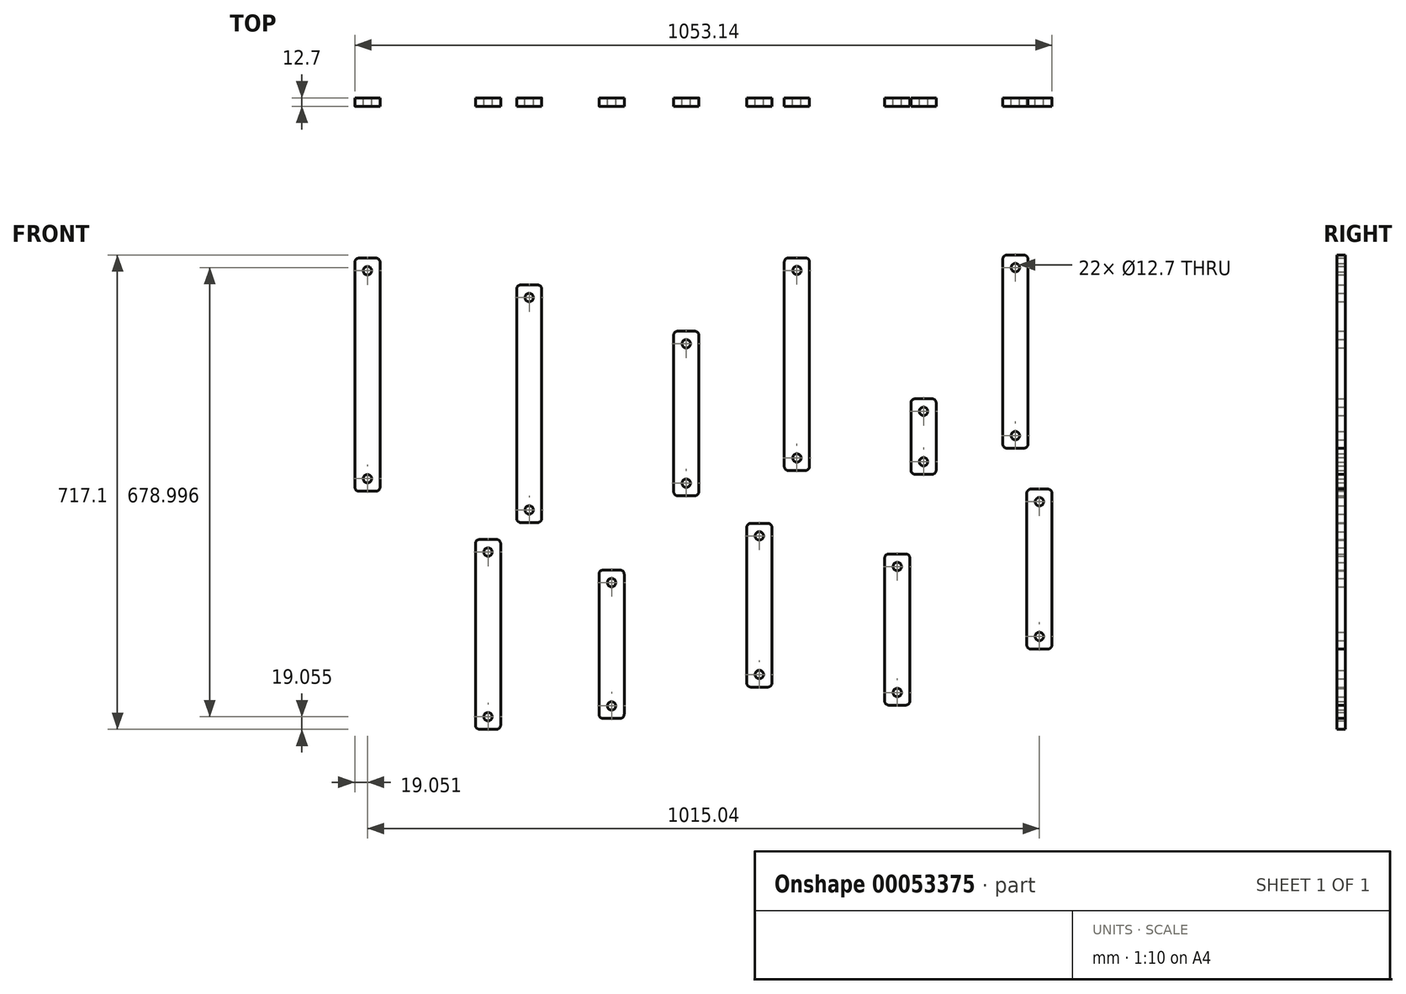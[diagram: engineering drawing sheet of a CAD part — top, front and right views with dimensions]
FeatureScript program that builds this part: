
annotation { "Feature Type Name" : "Feature", "Feature Type Description" : "" }
export const myFeature = defineFeature(function(context is Context, id is Id, definition is map)
    precondition{}
    {
        {
            var Q0;
            Q0=qCreatedBy(makeId("Front.planeOp"),FACE);
            var sketch = newSketch(context, id + "F0", { "sketchPlane" : qUnion([Q0])});
            skCircle(sketch, "E0", {"center": v(-240.16, 160.13) * mm, "radius": 6.35 * mm});
            skCircle(sketch, "E1", {"center": v(-240.16, -93.87) * mm, "radius": 6.35 * mm});
            skLineSegment(sketch, "E2.bottom", {"start": v(-252.86, 179.18) * mm, "end": v(-227.46, 179.18) * mm});
            skLineSegment(sketch, "E2.top", {"start": v(-252.86, -112.92) * mm, "end": v(-227.46, -112.92) * mm});
            skLineSegment(sketch, "E2.left", {"start": v(-259.2, 172.83) * mm, "end": v(-259.2, -106.57) * mm});
            skLineSegment(sketch, "E2.right", {"start": v(-221.1, 172.83) * mm, "end": v(-221.1, -106.57) * mm});
            skPoint(sketch, "E3.visualSharp", {"position": v(-221.1, 179.18) * mm});
            skArc(sketch, "E3.filletArc", {"start": v(-221.1, 172.83) * mm, "mid": v(-222.97, 177.32) * mm, "end": v(-227.46, 179.18) * mm});
            skPoint(sketch, "E4.visualSharp", {"position": v(-259.2, 179.18) * mm});
            skArc(sketch, "E4.filletArc", {"start": v(-252.86, 179.18) * mm, "mid": v(-257.35, 177.32) * mm, "end": v(-259.2, 172.83) * mm});
            skPoint(sketch, "E5.visualSharp", {"position": v(-221.1, -112.92) * mm});
            skArc(sketch, "E5.filletArc", {"start": v(-227.46, -112.92) * mm, "mid": v(-222.97, -111.06) * mm, "end": v(-221.1, -106.57) * mm});
            skPoint(sketch, "E6.visualSharp", {"position": v(-259.2, -112.92) * mm});
            skArc(sketch, "E6.filletArc", {"start": v(-259.2, -106.57) * mm, "mid": v(-257.35, -111.06) * mm, "end": v(-252.86, -112.92) * mm});
            skLineSegment(sketch, "E7.right", {"start": v(-359.88, -44.47) * mm, "end": v(-359.88, -146.07) * mm});
            skLineSegment(sketch, "E7.left", {"start": v(-397.98, -44.47) * mm, "end": v(-397.98, -146.07) * mm});
            skPoint(sketch, "E8.visualSharp", {"position": v(-359.88, -38.12) * mm});
            skLineSegment(sketch, "E7.top", {"start": v(-391.63, -152.42) * mm, "end": v(-366.23, -152.42) * mm});
            skLineSegment(sketch, "E7.bottom", {"start": v(-391.63, -38.12) * mm, "end": v(-366.23, -38.12) * mm});
            skPoint(sketch, "E9.visualSharp", {"position": v(-397.98, -38.12) * mm});
            skCircle(sketch, "E10", {"center": v(-378.93, -133.37) * mm, "radius": 6.35 * mm});
            skCircle(sketch, "E11", {"center": v(-378.93, -57.17) * mm, "radius": 6.35 * mm});
            skPoint(sketch, "E12.visualSharp", {"position": v(-359.88, -152.42) * mm});
            skPoint(sketch, "E13.visualSharp", {"position": v(-397.98, -152.42) * mm});
            skArc(sketch, "E12.filletArc", {"start": v(-366.23, -152.42) * mm, "mid": v(-361.74, -150.56) * mm, "end": v(-359.88, -146.07) * mm});
            skArc(sketch, "E9.filletArc", {"start": v(-391.63, -38.12) * mm, "mid": v(-396.12, -39.98) * mm, "end": v(-397.98, -44.47) * mm});
            skArc(sketch, "E8.filletArc", {"start": v(-359.88, -44.47) * mm, "mid": v(-361.74, -39.98) * mm, "end": v(-366.23, -38.12) * mm});
            skArc(sketch, "E13.filletArc", {"start": v(-397.98, -146.07) * mm, "mid": v(-396.12, -150.56) * mm, "end": v(-391.63, -152.42) * mm});
            skPoint(sketch, "E14.visualSharp", {"position": v(-589.26, -146.73) * mm});
            skPoint(sketch, "E15.visualSharp", {"position": v(-551.16, -146.73) * mm});
            skPoint(sketch, "E16.visualSharp", {"position": v(-589.26, 174.84) * mm});
            skLineSegment(sketch, "E17.left", {"start": v(-589.26, 168.49) * mm, "end": v(-589.26, -140.38) * mm});
            skLineSegment(sketch, "E17.right", {"start": v(-551.16, 168.49) * mm, "end": v(-551.16, -140.38) * mm});
            skPoint(sketch, "E18.visualSharp", {"position": v(-551.16, 174.84) * mm});
            skCircle(sketch, "E19", {"center": v(-570.2, 155.79) * mm, "radius": 6.35 * mm});
            skLineSegment(sketch, "E17.top", {"start": v(-582.9, -146.73) * mm, "end": v(-557.5, -146.73) * mm});
            skCircle(sketch, "E20", {"center": v(-570.2, -127.68) * mm, "radius": 6.35 * mm});
            skLineSegment(sketch, "E17.bottom", {"start": v(-582.9, 174.84) * mm, "end": v(-557.5, 174.84) * mm});
            skArc(sketch, "E16.filletArc", {"start": v(-582.9, 174.84) * mm, "mid": v(-587.4, 172.98) * mm, "end": v(-589.26, 168.49) * mm});
            skArc(sketch, "E18.filletArc", {"start": v(-551.16, 168.49) * mm, "mid": v(-553.02, 172.98) * mm, "end": v(-557.5, 174.84) * mm});
            skArc(sketch, "E15.filletArc", {"start": v(-557.5, -146.73) * mm, "mid": v(-553.02, -144.87) * mm, "end": v(-551.16, -140.38) * mm});
            skArc(sketch, "E14.filletArc", {"start": v(-589.26, -140.38) * mm, "mid": v(-587.4, -144.87) * mm, "end": v(-582.9, -146.73) * mm});
            skPoint(sketch, "E21.visualSharp", {"position": v(-756.47, -184.84) * mm});
            skPoint(sketch, "E22.visualSharp", {"position": v(-718.37, -184.84) * mm});
            skPoint(sketch, "E23.visualSharp", {"position": v(-756.47, 64.08) * mm});
            skLineSegment(sketch, "E24.left", {"start": v(-756.47, 57.73) * mm, "end": v(-756.47, -178.49) * mm});
            skLineSegment(sketch, "E24.right", {"start": v(-718.37, 57.73) * mm, "end": v(-718.37, -178.49) * mm});
            skPoint(sketch, "E25.visualSharp", {"position": v(-718.37, 64.08) * mm});
            skCircle(sketch, "E26", {"center": v(-737.42, 45.03) * mm, "radius": 6.35 * mm});
            skLineSegment(sketch, "E24.top", {"start": v(-750.12, -184.84) * mm, "end": v(-724.72, -184.84) * mm});
            skCircle(sketch, "E27", {"center": v(-737.42, -165.79) * mm, "radius": 6.35 * mm});
            skLineSegment(sketch, "E24.bottom", {"start": v(-750.12, 64.08) * mm, "end": v(-724.72, 64.08) * mm});
            skArc(sketch, "E23.filletArc", {"start": v(-750.12, 64.08) * mm, "mid": v(-754.6, 62.22) * mm, "end": v(-756.47, 57.73) * mm});
            skArc(sketch, "E25.filletArc", {"start": v(-718.37, 57.73) * mm, "mid": v(-720.23, 62.22) * mm, "end": v(-724.72, 64.08) * mm});
            skArc(sketch, "E22.filletArc", {"start": v(-724.72, -184.84) * mm, "mid": v(-720.23, -182.98) * mm, "end": v(-718.37, -178.49) * mm});
            skArc(sketch, "E21.filletArc", {"start": v(-756.47, -178.49) * mm, "mid": v(-754.6, -182.98) * mm, "end": v(-750.12, -184.84) * mm});
            skPoint(sketch, "E28.visualSharp", {"position": v(-222.96, -416.6) * mm});
            skPoint(sketch, "E29.visualSharp", {"position": v(-184.86, -416.6) * mm});
            skPoint(sketch, "E30.visualSharp", {"position": v(-222.96, -174.78) * mm});
            skLineSegment(sketch, "E31.left", {"start": v(-222.96, -181.13) * mm, "end": v(-222.96, -410.24) * mm});
            skLineSegment(sketch, "E31.right", {"start": v(-184.86, -181.13) * mm, "end": v(-184.86, -410.24) * mm});
            skPoint(sketch, "E32.visualSharp", {"position": v(-184.86, -174.78) * mm});
            skCircle(sketch, "E33", {"center": v(-203.9, -193.83) * mm, "radius": 6.35 * mm});
            skLineSegment(sketch, "E31.top", {"start": v(-216.6, -416.6) * mm, "end": v(-191.2, -416.6) * mm});
            skCircle(sketch, "E34", {"center": v(-203.9, -397.54) * mm, "radius": 6.35 * mm});
            skLineSegment(sketch, "E31.bottom", {"start": v(-216.6, -174.78) * mm, "end": v(-191.2, -174.78) * mm});
            skArc(sketch, "E30.filletArc", {"start": v(-216.6, -174.78) * mm, "mid": v(-221.1, -176.64) * mm, "end": v(-222.96, -181.13) * mm});
            skArc(sketch, "E32.filletArc", {"start": v(-184.86, -181.13) * mm, "mid": v(-186.72, -176.64) * mm, "end": v(-191.2, -174.78) * mm});
            skArc(sketch, "E29.filletArc", {"start": v(-191.2, -416.6) * mm, "mid": v(-186.72, -414.73) * mm, "end": v(-184.86, -410.24) * mm});
            skArc(sketch, "E28.filletArc", {"start": v(-222.96, -410.24) * mm, "mid": v(-221.1, -414.73) * mm, "end": v(-216.6, -416.6) * mm});
            skPoint(sketch, "E35.visualSharp", {"position": v(-437.6, -501.36) * mm});
            skPoint(sketch, "E36.visualSharp", {"position": v(-399.5, -501.36) * mm});
            skPoint(sketch, "E37.visualSharp", {"position": v(-437.6, -272.76) * mm});
            skLineSegment(sketch, "E38.left", {"start": v(-437.6, -279.11) * mm, "end": v(-437.6, -495.01) * mm});
            skLineSegment(sketch, "E38.right", {"start": v(-399.5, -279.11) * mm, "end": v(-399.5, -495.01) * mm});
            skPoint(sketch, "E39.visualSharp", {"position": v(-399.5, -272.76) * mm});
            skCircle(sketch, "E40", {"center": v(-418.56, -291.81) * mm, "radius": 6.35 * mm});
            skLineSegment(sketch, "E38.top", {"start": v(-431.26, -501.36) * mm, "end": v(-405.86, -501.36) * mm});
            skCircle(sketch, "E41", {"center": v(-418.56, -482.31) * mm, "radius": 6.35 * mm});
            skLineSegment(sketch, "E38.bottom", {"start": v(-431.26, -272.76) * mm, "end": v(-405.86, -272.76) * mm});
            skArc(sketch, "E37.filletArc", {"start": v(-431.26, -272.76) * mm, "mid": v(-435.75, -274.62) * mm, "end": v(-437.6, -279.11) * mm});
            skArc(sketch, "E39.filletArc", {"start": v(-399.5, -279.11) * mm, "mid": v(-401.37, -274.62) * mm, "end": v(-405.86, -272.76) * mm});
            skArc(sketch, "E36.filletArc", {"start": v(-405.86, -501.36) * mm, "mid": v(-401.37, -499.5) * mm, "end": v(-399.5, -495.01) * mm});
            skArc(sketch, "E35.filletArc", {"start": v(-437.6, -495.01) * mm, "mid": v(-435.75, -499.5) * mm, "end": v(-431.26, -501.36) * mm});
            skPoint(sketch, "E42.visualSharp", {"position": v(-646.03, -474.14) * mm});
            skPoint(sketch, "E43.visualSharp", {"position": v(-607.93, -474.14) * mm});
            skPoint(sketch, "E44.visualSharp", {"position": v(-646.03, -226.5) * mm});
            skLineSegment(sketch, "E45.left", {"start": v(-646.03, -232.84) * mm, "end": v(-646.03, -467.8) * mm});
            skLineSegment(sketch, "E45.right", {"start": v(-607.93, -232.84) * mm, "end": v(-607.93, -467.8) * mm});
            skPoint(sketch, "E46.visualSharp", {"position": v(-607.93, -226.5) * mm});
            skCircle(sketch, "E47", {"center": v(-626.98, -245.54) * mm, "radius": 6.35 * mm});
            skLineSegment(sketch, "E45.top", {"start": v(-639.68, -474.14) * mm, "end": v(-614.28, -474.14) * mm});
            skCircle(sketch, "E48", {"center": v(-626.98, -455.1) * mm, "radius": 6.35 * mm});
            skLineSegment(sketch, "E45.bottom", {"start": v(-639.68, -226.5) * mm, "end": v(-614.28, -226.5) * mm});
            skArc(sketch, "E44.filletArc", {"start": v(-639.68, -226.5) * mm, "mid": v(-644.17, -228.35) * mm, "end": v(-646.03, -232.84) * mm});
            skArc(sketch, "E46.filletArc", {"start": v(-607.93, -232.84) * mm, "mid": v(-609.8, -228.35) * mm, "end": v(-614.28, -226.5) * mm});
            skArc(sketch, "E43.filletArc", {"start": v(-614.28, -474.14) * mm, "mid": v(-609.8, -472.28) * mm, "end": v(-607.93, -467.8) * mm});
            skArc(sketch, "E42.filletArc", {"start": v(-646.03, -467.8) * mm, "mid": v(-644.17, -472.28) * mm, "end": v(-639.68, -474.14) * mm});
            skPoint(sketch, "E49.visualSharp", {"position": v(-869.23, -521.58) * mm});
            skPoint(sketch, "E50.visualSharp", {"position": v(-831.13, -521.58) * mm});
            skPoint(sketch, "E51.visualSharp", {"position": v(-869.23, -297.05) * mm});
            skLineSegment(sketch, "E52.left", {"start": v(-869.23, -303.4) * mm, "end": v(-869.23, -515.23) * mm});
            skLineSegment(sketch, "E52.right", {"start": v(-831.13, -303.4) * mm, "end": v(-831.13, -515.23) * mm});
            skPoint(sketch, "E53.visualSharp", {"position": v(-831.13, -297.05) * mm});
            skCircle(sketch, "E54", {"center": v(-850.18, -316.1) * mm, "radius": 6.35 * mm});
            skLineSegment(sketch, "E52.top", {"start": v(-862.88, -521.58) * mm, "end": v(-837.48, -521.58) * mm});
            skCircle(sketch, "E55", {"center": v(-850.18, -502.53) * mm, "radius": 6.35 * mm});
            skLineSegment(sketch, "E52.bottom", {"start": v(-862.88, -297.05) * mm, "end": v(-837.48, -297.05) * mm});
            skArc(sketch, "E51.filletArc", {"start": v(-862.88, -297.05) * mm, "mid": v(-867.37, -298.9) * mm, "end": v(-869.23, -303.4) * mm});
            skArc(sketch, "E53.filletArc", {"start": v(-831.13, -303.4) * mm, "mid": v(-833, -298.9) * mm, "end": v(-837.48, -297.05) * mm});
            skArc(sketch, "E50.filletArc", {"start": v(-837.48, -521.58) * mm, "mid": v(-833, -519.72) * mm, "end": v(-831.13, -515.23) * mm});
            skArc(sketch, "E49.filletArc", {"start": v(-869.23, -515.23) * mm, "mid": v(-867.37, -519.72) * mm, "end": v(-862.88, -521.58) * mm});
            skPoint(sketch, "E56.visualSharp", {"position": v(-993.67, -225.28) * mm});
            skPoint(sketch, "E57.visualSharp", {"position": v(-955.57, -225.28) * mm});
            skPoint(sketch, "E58.visualSharp", {"position": v(-993.67, 133.88) * mm});
            skLineSegment(sketch, "E59.left", {"start": v(-993.67, 127.53) * mm, "end": v(-993.67, -218.93) * mm});
            skLineSegment(sketch, "E59.right", {"start": v(-955.57, 127.53) * mm, "end": v(-955.57, -218.93) * mm});
            skPoint(sketch, "E60.visualSharp", {"position": v(-955.57, 133.88) * mm});
            skCircle(sketch, "E61", {"center": v(-974.62, 114.83) * mm, "radius": 6.35 * mm});
            skLineSegment(sketch, "E59.top", {"start": v(-987.32, -225.28) * mm, "end": v(-961.92, -225.28) * mm});
            skCircle(sketch, "E62", {"center": v(-974.62, -206.23) * mm, "radius": 6.35 * mm});
            skLineSegment(sketch, "E59.bottom", {"start": v(-987.32, 133.88) * mm, "end": v(-961.92, 133.88) * mm});
            skArc(sketch, "E58.filletArc", {"start": v(-987.32, 133.88) * mm, "mid": v(-991.8, 132.02) * mm, "end": v(-993.67, 127.53) * mm});
            skArc(sketch, "E60.filletArc", {"start": v(-955.57, 127.53) * mm, "mid": v(-957.43, 132.02) * mm, "end": v(-961.92, 133.88) * mm});
            skArc(sketch, "E57.filletArc", {"start": v(-961.92, -225.28) * mm, "mid": v(-957.43, -223.42) * mm, "end": v(-955.57, -218.93) * mm});
            skArc(sketch, "E56.filletArc", {"start": v(-993.67, -218.93) * mm, "mid": v(-991.8, -223.42) * mm, "end": v(-987.32, -225.28) * mm});
            skPoint(sketch, "E63.visualSharp", {"position": v(-1055.88, -537.92) * mm});
            skPoint(sketch, "E64.visualSharp", {"position": v(-1017.78, -537.92) * mm});
            skPoint(sketch, "E65.visualSharp", {"position": v(-1055.88, -250.9) * mm});
            skLineSegment(sketch, "E66.left", {"start": v(-1055.88, -257.25) * mm, "end": v(-1055.88, -531.57) * mm});
            skLineSegment(sketch, "E66.right", {"start": v(-1017.78, -257.25) * mm, "end": v(-1017.78, -531.57) * mm});
            skPoint(sketch, "E67.visualSharp", {"position": v(-1017.78, -250.9) * mm});
            skCircle(sketch, "E68", {"center": v(-1036.83, -269.95) * mm, "radius": 6.35 * mm});
            skLineSegment(sketch, "E66.top", {"start": v(-1049.53, -537.92) * mm, "end": v(-1024.13, -537.92) * mm});
            skCircle(sketch, "E69", {"center": v(-1036.83, -518.87) * mm, "radius": 6.35 * mm});
            skLineSegment(sketch, "E66.bottom", {"start": v(-1049.53, -250.9) * mm, "end": v(-1024.13, -250.9) * mm});
            skArc(sketch, "E65.filletArc", {"start": v(-1049.53, -250.9) * mm, "mid": v(-1054.02, -252.76) * mm, "end": v(-1055.88, -257.25) * mm});
            skArc(sketch, "E67.filletArc", {"start": v(-1017.78, -257.25) * mm, "mid": v(-1019.64, -252.76) * mm, "end": v(-1024.13, -250.9) * mm});
            skArc(sketch, "E64.filletArc", {"start": v(-1024.13, -537.92) * mm, "mid": v(-1019.64, -536.06) * mm, "end": v(-1017.78, -531.57) * mm});
            skArc(sketch, "E63.filletArc", {"start": v(-1055.88, -531.57) * mm, "mid": v(-1054.02, -536.06) * mm, "end": v(-1049.53, -537.92) * mm});
            skPoint(sketch, "E70.visualSharp", {"position": v(-1238, -178.06) * mm});
            skPoint(sketch, "E71.visualSharp", {"position": v(-1199.9, -178.06) * mm});
            skPoint(sketch, "E72.visualSharp", {"position": v(-1238, 174.5) * mm});
            skLineSegment(sketch, "E73.left", {"start": v(-1238, 168.15) * mm, "end": v(-1238, -171.7) * mm});
            skLineSegment(sketch, "E73.right", {"start": v(-1199.9, 168.15) * mm, "end": v(-1199.9, -171.7) * mm});
            skPoint(sketch, "E74.visualSharp", {"position": v(-1199.9, 174.5) * mm});
            skCircle(sketch, "E75", {"center": v(-1218.95, 155.45) * mm, "radius": 6.35 * mm});
            skLineSegment(sketch, "E73.top", {"start": v(-1231.65, -178.06) * mm, "end": v(-1206.25, -178.06) * mm});
            skCircle(sketch, "E76", {"center": v(-1218.95, -159) * mm, "radius": 6.35 * mm});
            skLineSegment(sketch, "E73.bottom", {"start": v(-1231.65, 174.5) * mm, "end": v(-1206.25, 174.5) * mm});
            skArc(sketch, "E72.filletArc", {"start": v(-1231.65, 174.5) * mm, "mid": v(-1236.14, 172.64) * mm, "end": v(-1238, 168.15) * mm});
            skArc(sketch, "E74.filletArc", {"start": v(-1199.9, 168.15) * mm, "mid": v(-1201.76, 172.64) * mm, "end": v(-1206.25, 174.5) * mm});
            skArc(sketch, "E71.filletArc", {"start": v(-1206.25, -178.06) * mm, "mid": v(-1201.76, -176.2) * mm, "end": v(-1199.9, -171.7) * mm});
            skArc(sketch, "E70.filletArc", {"start": v(-1238, -171.7) * mm, "mid": v(-1236.14, -176.2) * mm, "end": v(-1231.65, -178.06) * mm});
            skSolve(sketch);
        }
        {
            var Q0;
            Q0=makeQuery(id+"F0.imprint","IMPRINT",FACE,{"disambiguationData":[TD([[makeQuery(id+"F0.imprint","IMPRINT",EDGE,{"derivedFrom":sQuery(id+"F0.wireOp",EDGE,"E73.left")}),1.0]])]});
            var Q1;
            Q1=makeQuery(id+"F0.imprint","IMPRINT",FACE,{"disambiguationData":[TD([[makeQuery(id+"F0.imprint","IMPRINT",EDGE,{"derivedFrom":sQuery(id+"F0.wireOp",EDGE,"E59.left")}),1.0]])]});
            var Q2;
            Q2=makeQuery(id+"F0.imprint","IMPRINT",FACE,{"disambiguationData":[TD([[makeQuery(id+"F0.imprint","IMPRINT",EDGE,{"derivedFrom":sQuery(id+"F0.wireOp",EDGE,"E24.left")}),1.0]])]});
            var Q3;
            Q3=makeQuery(id+"F0.imprint","IMPRINT",FACE,{"disambiguationData":[TD([[makeQuery(id+"F0.imprint","IMPRINT",EDGE,{"derivedFrom":sQuery(id+"F0.wireOp",EDGE,"E17.left")}),1.0]])]});
            var Q4;
            Q4=makeQuery(id+"F0.imprint","IMPRINT",FACE,{"disambiguationData":[TD([[makeQuery(id+"F0.imprint","IMPRINT",EDGE,{"derivedFrom":sQuery(id+"F0.wireOp",EDGE,"E7.right")}),-1.0]])]});
            var Q5;
            Q5=makeQuery(id+"F0.imprint","IMPRINT",FACE,{"disambiguationData":[TD([[makeQuery(id+"F0.imprint","IMPRINT",EDGE,{"derivedFrom":sQuery(id+"F0.wireOp",EDGE,"E0")}),-1.0]])]});
            var Q6;
            Q6=makeQuery(id+"F0.imprint","IMPRINT",FACE,{"disambiguationData":[TD([[makeQuery(id+"F0.imprint","IMPRINT",EDGE,{"derivedFrom":sQuery(id+"F0.wireOp",EDGE,"E31.left")}),1.0]])]});
            var Q7;
            Q7=makeQuery(id+"F0.imprint","IMPRINT",FACE,{"disambiguationData":[TD([[makeQuery(id+"F0.imprint","IMPRINT",EDGE,{"derivedFrom":sQuery(id+"F0.wireOp",EDGE,"E38.left")}),1.0]])]});
            var Q8;
            Q8=makeQuery(id+"F0.imprint","IMPRINT",FACE,{"disambiguationData":[TD([[makeQuery(id+"F0.imprint","IMPRINT",EDGE,{"derivedFrom":sQuery(id+"F0.wireOp",EDGE,"E45.left")}),1.0]])]});
            var Q9;
            Q9=makeQuery(id+"F0.imprint","IMPRINT",FACE,{"disambiguationData":[TD([[makeQuery(id+"F0.imprint","IMPRINT",EDGE,{"derivedFrom":sQuery(id+"F0.wireOp",EDGE,"E52.left")}),1.0]])]});
            var Q10;
            Q10=makeQuery(id+"F0.imprint","IMPRINT",FACE,{"disambiguationData":[TD([[makeQuery(id+"F0.imprint","IMPRINT",EDGE,{"derivedFrom":sQuery(id+"F0.wireOp",EDGE,"E66.left")}),1.0]])]});
            extrude(context, id + "F1", {"entities" : qUnion([Q0, Q1, Q2, Q3, Q4, Q5, Q6, Q7, Q8, Q9, Q10]), "depth" : 12.7 * mm});
        }
    });
